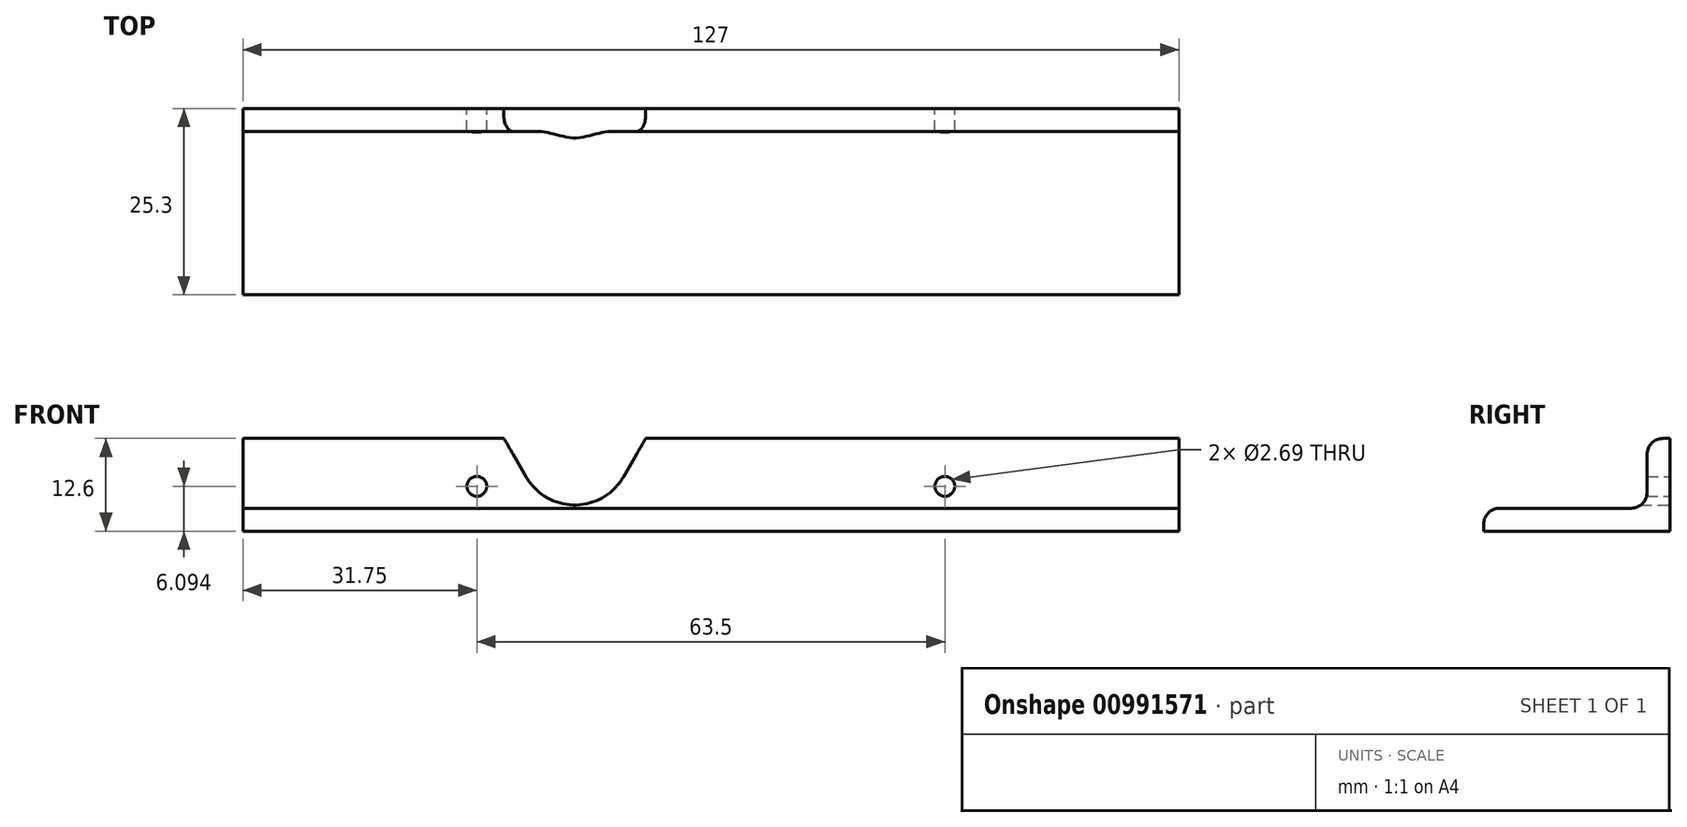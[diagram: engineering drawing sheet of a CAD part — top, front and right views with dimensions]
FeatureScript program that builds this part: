
annotation { "Feature Type Name" : "Feature", "Feature Type Description" : "" }
export const myFeature = defineFeature(function(context is Context, id is Id, definition is map)
    precondition{}
    {
        {
            var Q0;
            Q0=qCreatedBy(makeId("Right.planeOp"),FACE);
            var sketch = newSketch(context, id + "F0", { "sketchPlane" : qUnion([Q0])});
            skLineSegment(sketch, "E0", {"start": v(-10.29, -8.26) * mm, "end": v(15.01, -8.26) * mm});
            skLineSegment(sketch, "E1", {"start": v(15.01, -8.26) * mm, "end": v(15.01, 4.34) * mm});
            skLineSegment(sketch, "E2", {"start": v(15.01, 4.34) * mm, "end": v(14.05, 4.34) * mm});
            skLineSegment(sketch, "E3", {"start": v(11.89, 2.18) * mm, "end": v(11.89, -2.98) * mm});
            skLineSegment(sketch, "E4", {"start": v(9.73, -5.14) * mm, "end": v(-8.13, -5.14) * mm});
            skLineSegment(sketch, "E5", {"start": v(-10.29, -7.3) * mm, "end": v(-10.29, -8.26) * mm});
            skPoint(sketch, "E6.visualSharp", {"position": v(-10.29, -5.14) * mm});
            skArc(sketch, "E6.filletArc", {"start": v(-8.13, -5.14) * mm, "mid": v(-9.65, -5.77) * mm, "end": v(-10.29, -7.3) * mm});
            skPoint(sketch, "E7.visualSharp", {"position": v(11.89, 4.34) * mm});
            skArc(sketch, "E7.filletArc", {"start": v(14.05, 4.34) * mm, "mid": v(12.52, 3.7) * mm, "end": v(11.89, 2.18) * mm});
            skPoint(sketch, "E8.visualSharp", {"position": v(11.89, -5.14) * mm});
            skArc(sketch, "E8.filletArc", {"start": v(9.73, -5.14) * mm, "mid": v(11.26, -4.5) * mm, "end": v(11.89, -2.98) * mm});
            skSolve(sketch);
        }
        {
            var Q0;
            Q0=qSketchRegion(id+"F0",true);
            extrude(context, id + "F1", {"entities" : qUnion([Q0]), "depth" : 127 * mm, "offsetDistance" : 25.4 * mm});
        }
        {
            var Q0;
            Q0=makeQuery(id+"F1.opExtrude","SWEPT_FACE",FACE,{"disambiguationData":[OSD([sQuery(id+"F0.wireOp",EDGE,"E1")])]});
            var sketch = newSketch(context, id + "F2", { "sketchPlane" : qUnion([Q0])});
            skCircle(sketch, "E9", {"center": v(-31.75, -2.17) * mm, "radius": 1.35 * mm});
            skCircle(sketch, "E10", {"center": v(-95.25, -2.17) * mm, "radius": 1.35 * mm});
            skSolve(sketch);
        }
        {
            var Q0;
            Q0=qSketchRegion(id+"F2",true);
            extrude(context, id + "F3", {"entities" : qUnion([Q0]), "operationType" : NewBodyOperationType.REMOVE, "endBound" : BoundingType.THROUGH_ALL, "oppositeDirection" : true, "depth" : 25.4 * mm, "offsetDistance" : 25.4 * mm});
        }
        {
            var Q0;
            Q0=makeQuery(id+"F1.opExtrude","SWEPT_FACE",FACE,{"disambiguationData":[OSD([sQuery(id+"F0.wireOp",EDGE,"E1")])]});
            var sketch = newSketch(context, id + "F4", { "sketchPlane" : qUnion([Q0])});
            skArc(sketch, "E11", {"start": v(-51.64, -0.9) * mm, "mid": v(-45.04, -4.7) * mm, "end": v(-38.44, -0.9) * mm});
            skLineSegment(sketch, "E12", {"start": v(-51.64, -0.9) * mm, "end": v(-54.66, 4.34) * mm});
            skLineSegment(sketch, "E13", {"start": v(-38.44, -0.9) * mm, "end": v(-35.42, 4.34) * mm});
            skSolve(sketch);
        }
        {
            var Q0;
            Q0 = qSketchRegion(id + "F4", true);
            var Q1;
            Q1=makeQuery(id+"F4.imprint","IMPRINT",FACE,{"disambiguationData":[TD([[makeQuery(id+"F4.imprint","IMPRINT",EDGE,{"derivedFrom":sQuery(id+"F4.wireOp",EDGE,"E11")}),1.0]])]});
            extrude(context, id + "F5", {"entities" : qUnion([Q0, Q1]), "operationType" : NewBodyOperationType.REMOVE, "endBound" : BoundingType.THROUGH_ALL, "oppositeDirection" : true, "depth" : 25.4 * mm, "offsetDistance" : 25.4 * mm});
        }
    });
